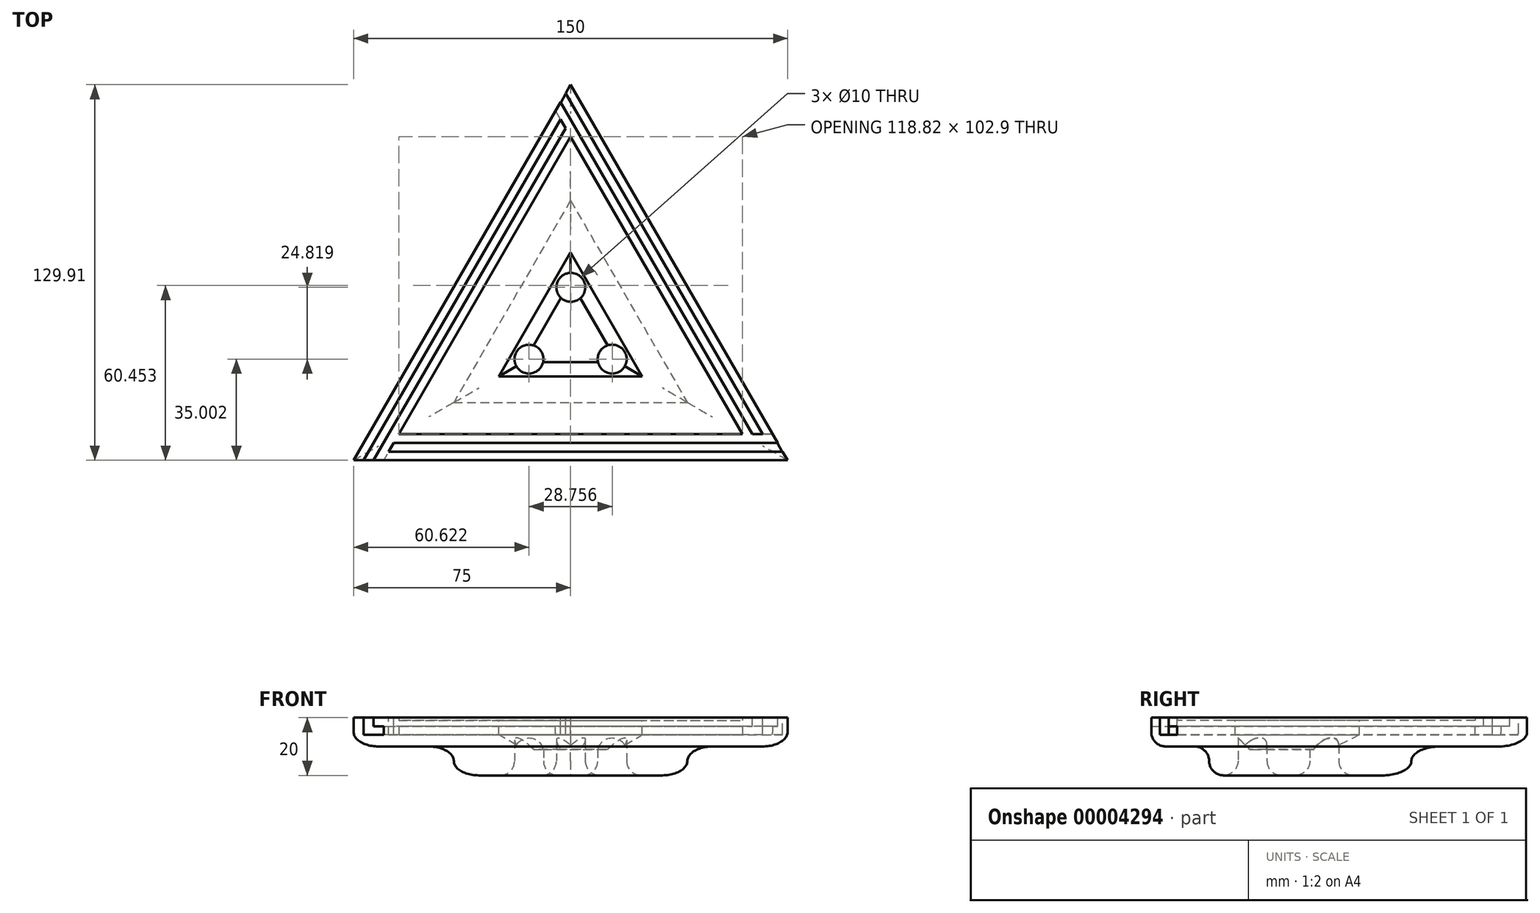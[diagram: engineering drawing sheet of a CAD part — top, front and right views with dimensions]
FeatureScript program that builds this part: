
annotation { "Feature Type Name" : "Feature", "Feature Type Description" : "" }
export const myFeature = defineFeature(function(context is Context, id is Id, definition is map)
    precondition{}
    {
        {
            var Q0;
            Q0=qCreatedBy(makeId("Top.planeOp"),FACE);
            var sketch = newSketch(context, id + "F0", { "sketchPlane" : qUnion([Q0])});
            skLineSegment(sketch, "E0.0", {"start": v(-75, -54.93) * mm, "end": v(75, -54.93) * mm});
            skLineSegment(sketch, "E1", {"start": v(0, 74.98) * mm, "end": v(-75, -54.93) * mm});
            skLineSegment(sketch, "E2", {"start": v(0, 74.98) * mm, "end": v(75, -54.93) * mm});
            skSolve(sketch);
        }
        {
            var Q0;
            Q0=makeQuery(id+"F0.imprint","IMPRINT",FACE,{"disambiguationData":[TD([[makeQuery(id+"F0.imprint","IMPRINT",EDGE,{"derivedFrom":sQuery(id+"F0.wireOp",EDGE,"E0.0")}),1.0]])]});
            extrude(context, id + "F1", {"entities" : qUnion([Q0]), "depth" : 10 * mm});
        }
        {
            var Q0;
            Q0=makeQuery(id+"F1.opExtrude","CAP_FACE",FACE,{"disambiguationData":[OSD([sQuery(id+"F0.wireOp",EDGE,"E0.0"),sQuery(id+"F0.wireOp",EDGE,"E1"),sQuery(id+"F0.wireOp",EDGE,"E2")])],"isStart":true});
            var sketch = newSketch(context, id + "F2", { "sketchPlane" : qUnion([Q0])});
            skLineSegment(sketch, "E3.0", {"start": v(-40.36, 34.93) * mm, "end": v(40.36, 34.93) * mm});
            skLineSegment(sketch, "E3.1", {"start": v(0, -34.98) * mm, "end": v(-40.36, 34.93) * mm});
            skLineSegment(sketch, "E3.2", {"start": v(0, -34.98) * mm, "end": v(40.36, 34.93) * mm});
            skSolve(sketch);
        }
        {
            var Q0;
            Q0=makeQuery(id+"F2.imprint","IMPRINT",FACE,{"disambiguationData":[TD([[makeQuery(id+"F2.imprint","IMPRINT",EDGE,{"derivedFrom":sQuery(id+"F2.wireOp",EDGE,"E3.0")}),-1.0]])]});
            extrude(context, id + "F3", {"entities" : qUnion([Q0]), "operationType" : NewBodyOperationType.ADD, "depth" : 10 * mm});
        }
        {
            var Q0;
            Q0=makeQuery(id+"F1.opExtrude","CAP_FACE",FACE,{"disambiguationData":[OSD([sQuery(id+"F0.wireOp",EDGE,"E0.0"),sQuery(id+"F0.wireOp",EDGE,"E1"),sQuery(id+"F0.wireOp",EDGE,"E2")])],"isStart":false});
            shell(context, id + "F4", {"entities" : qUnion([Q0]), "thickness" : 9 * mm});
        }
        {
            var Q0;
            Q0=makeQuery(id+"F1.opExtrude","CAP_FACE",FACE,{"disambiguationData":[OSD([sQuery(id+"F0.wireOp",EDGE,"E0.0"),sQuery(id+"F0.wireOp",EDGE,"E1"),sQuery(id+"F0.wireOp",EDGE,"E2")])],"isStart":false});
            var sketch = newSketch(context, id + "F5", { "sketchPlane" : qUnion([Q0])});
            skLineSegment(sketch, "E4", {"start": v(75, -54.93) * mm, "end": v(0, 74.98) * mm});
            skLineSegment(sketch, "E5", {"start": v(0, 74.98) * mm, "end": v(-75, -54.93) * mm});
            skLineSegment(sketch, "E6", {"start": v(-75, -54.93) * mm, "end": v(75, -54.93) * mm});
            skLineSegment(sketch, "E7.0", {"start": v(71.54, -54.93) * mm, "end": v(-1.73, 71.98) * mm});
            skLineSegment(sketch, "E8.0", {"start": v(1.73, 71.98) * mm, "end": v(-71.54, -54.93) * mm});
            skLineSegment(sketch, "E9.0", {"start": v(-73.27, -51.93) * mm, "end": v(73.27, -51.93) * mm});
            skLineSegment(sketch, "E10.0", {"start": v(-71.54, -48.93) * mm, "end": v(71.54, -48.93) * mm});
            skLineSegment(sketch, "E11.0", {"start": v(3.46, 68.98) * mm, "end": v(-68.07, -54.93) * mm});
            skLineSegment(sketch, "E12.0", {"start": v(68.07, -54.93) * mm, "end": v(-3.46, 68.98) * mm});
            skLineSegment(sketch, "E13", {"start": v(5.01, 66.3) * mm, "end": v(-64.58, -54.93) * mm});
            skLineSegment(sketch, "E14", {"start": v(-59.41, -45.93) * mm, "end": v(59.41, -45.93) * mm});
            skLineSegment(sketch, "E15", {"start": v(69.8, -45.93) * mm, "end": v(-69.8, -45.93) * mm});
            skLineSegment(sketch, "E16.0", {"start": v(64.6, -54.93) * mm, "end": v(-6.21, 67.74) * mm});
            skSolve(sketch);
        }
        {
            var Q0;
            {var subQ3=sQuery(id+"F5.wireOp",EDGE,"E4");var subQ5=sQuery(id+"F5.wireOp",EDGE,"E9.0");var subQ7=makeQuery(id+"F5.imprint","INTERSECT",VERTEX,{"derivedFrom":[subQ3,subQ5]});Q0=makeQuery(id+"F5.imprint","IMPRINT",FACE,{"disambiguationData":[TD([[makeQuery(id+"F5.imprint","IMPRINT",EDGE,{"disambiguationData":[TD([[subQ7,1.0]])],"derivedFrom":subQ3}),-1.0]])]});}
            var Q1;
            {var subQ3=sQuery(id+"F5.wireOp",EDGE,"E9.0");var subQ5=sQuery(id+"F5.wireOp",EDGE,"E7.0");var subQ7=makeQuery(id+"F5.imprint","INTERSECT",VERTEX,{"derivedFrom":[subQ5,subQ3]});Q1=makeQuery(id+"F5.imprint","IMPRINT",FACE,{"disambiguationData":[TD([[makeQuery(id+"F5.imprint","IMPRINT",EDGE,{"disambiguationData":[TD([[subQ7,-1.0]])],"derivedFrom":subQ5}),1.0]])]});}
            var Q2;
            {var subQ0=sQuery(id+"F5.wireOp",EDGE,"E16.0");var subQ3=sQuery(id+"F5.wireOp",EDGE,"E9.0");var subQ4=makeQuery(id+"F5.imprint","INTERSECT",VERTEX,{"derivedFrom":[subQ3,subQ0]});Q2=makeQuery(id+"F5.imprint","IMPRINT",FACE,{"disambiguationData":[TD([[makeQuery(id+"F5.imprint","IMPRINT",EDGE,{"disambiguationData":[TD([[subQ4,-1.0]])],"derivedFrom":subQ3}),1.0]])]});}
            var Q3;
            {var subQ3=sQuery(id+"F5.wireOp",EDGE,"E9.0");var subQ5=sQuery(id+"F5.wireOp",EDGE,"E13");var subQ7=makeQuery(id+"F5.imprint","INTERSECT",VERTEX,{"derivedFrom":[subQ3,subQ5]});Q3=makeQuery(id+"F5.imprint","IMPRINT",FACE,{"disambiguationData":[TD([[makeQuery(id+"F5.imprint","IMPRINT",EDGE,{"disambiguationData":[TD([[subQ7,-1.0]])],"derivedFrom":subQ3}),1.0]])]});}
            var Q4;
            {var subQ3=sQuery(id+"F5.wireOp",EDGE,"E6");var subQ5=sQuery(id+"F5.wireOp",EDGE,"E8.0");var subQ7=makeQuery(id+"F5.imprint","INTERSECT",VERTEX,{"derivedFrom":[subQ3,subQ5]});Q4=makeQuery(id+"F5.imprint","IMPRINT",FACE,{"disambiguationData":[TD([[makeQuery(id+"F5.imprint","IMPRINT",EDGE,{"disambiguationData":[TD([[subQ7,-1.0]])],"derivedFrom":subQ3}),1.0]])]});}
            var Q5;
            {var subQ1=sQuery(id+"F5.wireOp",EDGE,"E10.0");var subQ5=sQuery(id+"F5.wireOp",EDGE,"E8.0");var subQ6=makeQuery(id+"F5.imprint","INTERSECT",VERTEX,{"derivedFrom":[subQ5,subQ1]});Q5=makeQuery(id+"F5.imprint","IMPRINT",FACE,{"disambiguationData":[TD([[makeQuery(id+"F5.imprint","IMPRINT",EDGE,{"disambiguationData":[TD([[subQ6,-1.0]])],"derivedFrom":subQ5}),1.0]])]});}
            var Q6;
            {var subQ0=sQuery(id+"F5.wireOp",EDGE,"E16.0");var subQ3=sQuery(id+"F5.wireOp",EDGE,"E8.0");var subQ4=makeQuery(id+"F5.imprint","INTERSECT",VERTEX,{"derivedFrom":[subQ3,subQ0]});Q6=makeQuery(id+"F5.imprint","IMPRINT",FACE,{"disambiguationData":[TD([[makeQuery(id+"F5.imprint","IMPRINT",EDGE,{"disambiguationData":[TD([[subQ4,-1.0]])],"derivedFrom":subQ3}),1.0]])]});}
            var Q7;
            {var subQ0=sQuery(id+"F5.wireOp",EDGE,"E15");var subQ3=sQuery(id+"F5.wireOp",EDGE,"E8.0");var subQ4=makeQuery(id+"F5.imprint","INTERSECT",VERTEX,{"derivedFrom":[subQ3,subQ0]});Q7=makeQuery(id+"F5.imprint","IMPRINT",FACE,{"disambiguationData":[TD([[makeQuery(id+"F5.imprint","IMPRINT",EDGE,{"disambiguationData":[TD([[subQ4,-1.0]])],"derivedFrom":subQ3}),1.0]])]});}
            var Q8;
            {var subQ3=sQuery(id+"F5.wireOp",EDGE,"E5");var subQ5=sQuery(id+"F5.wireOp",EDGE,"E7.0");var subQ7=makeQuery(id+"F5.imprint","INTERSECT",VERTEX,{"derivedFrom":[subQ3,subQ5]});Q8=makeQuery(id+"F5.imprint","IMPRINT",FACE,{"disambiguationData":[TD([[makeQuery(id+"F5.imprint","IMPRINT",EDGE,{"disambiguationData":[TD([[subQ7,-1.0]])],"derivedFrom":subQ3}),1.0]])]});}
            var Q9;
            {var subQ1=sQuery(id+"F5.wireOp",EDGE,"E11.0");var subQ5=sQuery(id+"F5.wireOp",EDGE,"E7.0");var subQ6=makeQuery(id+"F5.imprint","INTERSECT",VERTEX,{"derivedFrom":[subQ5,subQ1]});Q9=makeQuery(id+"F5.imprint","IMPRINT",FACE,{"disambiguationData":[TD([[makeQuery(id+"F5.imprint","IMPRINT",EDGE,{"disambiguationData":[TD([[subQ6,-1.0]])],"derivedFrom":subQ5}),1.0]])]});}
            var Q10;
            {var subQ0=sQuery(id+"F5.wireOp",EDGE,"E13");var subQ3=sQuery(id+"F5.wireOp",EDGE,"E7.0");var subQ4=makeQuery(id+"F5.imprint","INTERSECT",VERTEX,{"derivedFrom":[subQ3,subQ0]});Q10=makeQuery(id+"F5.imprint","IMPRINT",FACE,{"disambiguationData":[TD([[makeQuery(id+"F5.imprint","IMPRINT",EDGE,{"disambiguationData":[TD([[subQ4,-1.0]])],"derivedFrom":subQ3}),1.0]])]});}
            var Q11;
            {var subQ0=sQuery(id+"F5.wireOp",EDGE,"E15");var subQ3=sQuery(id+"F5.wireOp",EDGE,"E7.0");var subQ4=makeQuery(id+"F5.imprint","INTERSECT",VERTEX,{"derivedFrom":[subQ3,subQ0]});Q11=makeQuery(id+"F5.imprint","IMPRINT",FACE,{"disambiguationData":[TD([[makeQuery(id+"F5.imprint","IMPRINT",EDGE,{"disambiguationData":[TD([[subQ4,-1.0]])],"derivedFrom":subQ3}),1.0]])]});}
            extrude(context, id + "F6", {"entities" : qUnion([Q0, Q1, Q2, Q3, Q4, Q5, Q6, Q7, Q8, Q9, Q10, Q11]), "operationType" : NewBodyOperationType.REMOVE, "oppositeDirection" : true, "depth" : 6 * mm});
        }
        {
            var Q0;
            Q0=makeQuery(id+"F6.boolean.opBoolean","COPY",FACE,{"derivedFrom":makeQuery(id+"F6.opExtrude","SWEPT_FACE",FACE,{"disambiguationData":[OSD([sQuery(id+"F5.wireOp",EDGE,"E12.0")])]})});
            var sketch = newSketch(context, id + "F7", { "sketchPlane" : qUnion([Q0])});
            skLineSegment(sketch, "E17", {"start": v(61.47, 4) * mm, "end": v(-71.21, 4) * mm});
            skLineSegment(sketch, "E18.0", {"start": v(61.47, 7) * mm, "end": v(-71.21, 7) * mm});
            skSolve(sketch);
        }
        {
            var Q0;
            {var subQ3=sQuery(id+"F7.wireOp",EDGE,"E17");Q0=makeQuery(id+"F7.imprint","IMPRINT",FACE,{"disambiguationData":[TD([[makeQuery(id+"F7.imprint","IMPRINT",EDGE,{"derivedFrom":subQ3}),1.0]])]});}
            extrude(context, id + "F8", {"entities" : qUnion([Q0]), "operationType" : NewBodyOperationType.REMOVE, "oppositeDirection" : true, "depth" : 3 * mm});
        }
        {
            var Q0;
            Q0=makeQuery(id+"F6.boolean.opBoolean","COPY",FACE,{"derivedFrom":makeQuery(id+"F6.opExtrude","SWEPT_FACE",FACE,{"disambiguationData":[OSD([sQuery(id+"F5.wireOp",EDGE,"E10.0")])]})});
            var sketch = newSketch(context, id + "F9", { "sketchPlane" : qUnion([Q0])});
            skLineSegment(sketch, "E19", {"start": v(71.54, 4) * mm, "end": v(-61.13, 4) * mm});
            skLineSegment(sketch, "E20.0", {"start": v(71.54, 7) * mm, "end": v(-61.13, 7) * mm});
            skSolve(sketch);
        }
        {
            var Q0;
            {var subQ3=sQuery(id+"F9.wireOp",EDGE,"E19");Q0=makeQuery(id+"F9.imprint","IMPRINT",FACE,{"disambiguationData":[TD([[makeQuery(id+"F9.imprint","IMPRINT",EDGE,{"derivedFrom":subQ3}),1.0]])]});}
            extrude(context, id + "F10", {"entities" : qUnion([Q0]), "operationType" : NewBodyOperationType.REMOVE, "oppositeDirection" : true, "depth" : 3 * mm});
        }
        {
            var Q0;
            Q0=makeQuery(id+"F6.boolean.opBoolean","COPY",FACE,{"derivedFrom":makeQuery(id+"F6.opExtrude","SWEPT_FACE",FACE,{"disambiguationData":[OSD([sQuery(id+"F5.wireOp",EDGE,"E11.0")])]})});
            var sketch = newSketch(context, id + "F11", { "sketchPlane" : qUnion([Q0])});
            skLineSegment(sketch, "E21", {"start": v(81.6, 4) * mm, "end": v(-51.07, 4) * mm});
            skLineSegment(sketch, "E22.0", {"start": v(81.6, 7) * mm, "end": v(-51.07, 7) * mm});
            skSolve(sketch);
        }
        {
            var Q0;
            {var subQ4=sQuery(id+"F11.wireOp",EDGE,"E21");Q0=makeQuery(id+"F11.imprint","IMPRINT",FACE,{"disambiguationData":[TD([[makeQuery(id+"F11.imprint","IMPRINT",EDGE,{"derivedFrom":subQ4}),1.0]])]});}
            extrude(context, id + "F12", {"entities" : qUnion([Q0]), "operationType" : NewBodyOperationType.REMOVE, "oppositeDirection" : true, "depth" : 3 * mm});
        }
        {
            var Q0;
            Q0=makeQuery(id+"F3.opExtrude","CAP_FACE",FACE,{"disambiguationData":[OSD([sQuery(id+"F2.wireOp",EDGE,"E3.0"),sQuery(id+"F2.wireOp",EDGE,"E3.1"),sQuery(id+"F2.wireOp",EDGE,"E3.2")])],"isStart":false});
            var sketch = newSketch(context, id + "F13", { "sketchPlane" : qUnion([Q0])});
            skCircle(sketch, "E23", {"center": v(14.38, 19.93) * mm, "radius": 5 * mm});
            skCircle(sketch, "E24", {"center": v(-14.38, 19.93) * mm, "radius": 5 * mm});
            skCircle(sketch, "E25", {"center": v(0.1, -4.9) * mm, "radius": 5 * mm});
            skSolve(sketch);
        }
        {
            var Q0;
            Q0=makeQuery(id+"F13.imprint","IMPRINT",FACE,{"disambiguationData":[TD([[makeQuery(id+"F13.imprint","IMPRINT",EDGE,{"derivedFrom":sQuery(id+"F13.wireOp",EDGE,"E24")}),1.0]])]});
            var Q1;
            Q1=makeQuery(id+"F13.imprint","IMPRINT",FACE,{"disambiguationData":[TD([[makeQuery(id+"F13.imprint","IMPRINT",EDGE,{"derivedFrom":sQuery(id+"F13.wireOp",EDGE,"E25")}),1.0]])]});
            var Q2;
            Q2=makeQuery(id+"F13.imprint","IMPRINT",FACE,{"disambiguationData":[TD([[makeQuery(id+"F13.imprint","IMPRINT",EDGE,{"derivedFrom":sQuery(id+"F13.wireOp",EDGE,"E23")}),1.0]])]});
            extrude(context, id + "F14", {"entities" : qUnion([Q0, Q1, Q2]), "operationType" : NewBodyOperationType.REMOVE, "oppositeDirection" : true, "depth" : 25 * mm});
        }
        {
            var Q0;
            Q0=makeQuery(id+"F1.opExtrude","CAP_EDGE",EDGE,{"disambiguationData":[OSD([sQuery(id+"F0.wireOp",EDGE,"E2")])],"isStart":true});
            var Q1;
            Q1=makeQuery(id+"F1.opExtrude","CAP_FACE",FACE,{"disambiguationData":[OSD([sQuery(id+"F0.wireOp",EDGE,"E0.0"),sQuery(id+"F0.wireOp",EDGE,"E1"),sQuery(id+"F0.wireOp",EDGE,"E2")])],"isStart":true});
            fillet(context, id + "F15", {"entities" : qUnion([Q0, Q1]), "radius" : 5 * mm, "tangentPropagation" : true, "allowEdgeOverflow" : false});
        }
        {
            var Q0;
            Q0=makeQuery(id+"F3.opExtrude","CAP_EDGE",EDGE,{"disambiguationData":[OSD([sQuery(id+"F2.wireOp",EDGE,"E3.0")])],"isStart":false});
            var Q1;
            Q1=makeQuery(id+"F3.opExtrude","CAP_FACE",FACE,{"disambiguationData":[OSD([sQuery(id+"F2.wireOp",EDGE,"E3.0"),sQuery(id+"F2.wireOp",EDGE,"E3.1"),sQuery(id+"F2.wireOp",EDGE,"E3.2")])],"isStart":false});
            fillet(context, id + "F16", {"entities" : qUnion([Q0, Q1]), "radius" : 5 * mm, "tangentPropagation" : true, "allowEdgeOverflow" : false});
        }
        {
            var Q0;
            {var subQ0=sQuery(id+"F2.wireOp",EDGE,"E3.1");Q0=makeQuery(id+"F4.opShell","OFFSET_EDGE",EDGE,{"disambiguationData":[OSD([subQ0]),TDD([makeQuery(id+"F3.opExtrude","CAP_EDGE",EDGE,{"disambiguationData":[OSD([subQ0])],"isStart":true})])]});}
            var Q1;
            {var subQ0=sQuery(id+"F2.wireOp",EDGE,"E3.0");Q1=makeQuery(id+"F4.opShell","OFFSET_EDGE",EDGE,{"disambiguationData":[OSD([subQ0]),TDD([makeQuery(id+"F3.opExtrude","CAP_EDGE",EDGE,{"disambiguationData":[OSD([subQ0])],"isStart":true})])]});}
            var Q2;
            {var subQ0=sQuery(id+"F2.wireOp",EDGE,"E3.2");Q2=makeQuery(id+"F4.opShell","OFFSET_EDGE",EDGE,{"disambiguationData":[OSD([subQ0]),TDD([makeQuery(id+"F3.opExtrude","CAP_EDGE",EDGE,{"disambiguationData":[OSD([subQ0])],"isStart":true})])]});}
            chamfer(context, id + "F17", {"entities" : qUnion([Q0, Q1, Q2]), "width" : 5 * mm, "tangentPropagation" : true});
        }
    });
